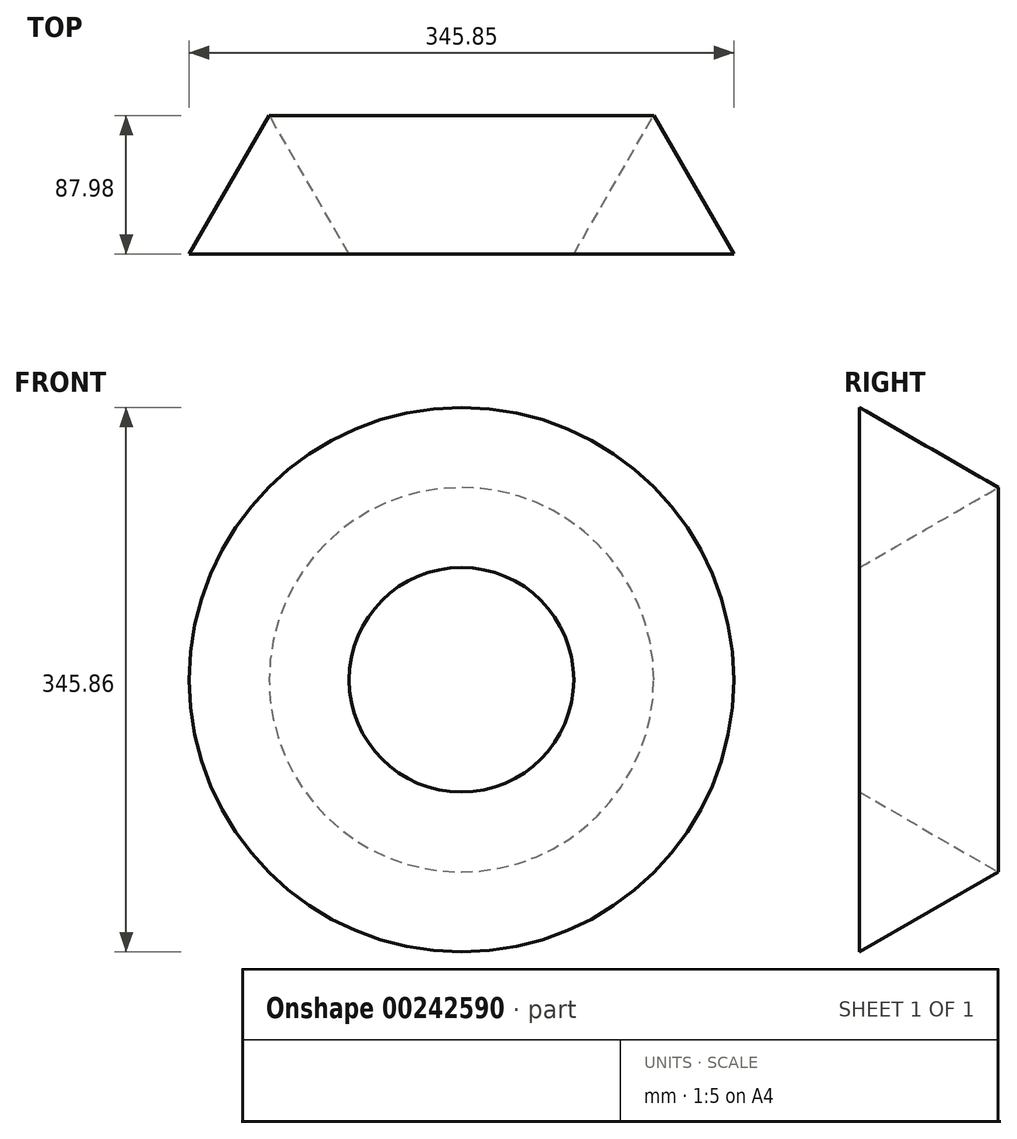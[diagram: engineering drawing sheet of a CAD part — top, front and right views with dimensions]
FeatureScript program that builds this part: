
annotation { "Feature Type Name" : "Feature", "Feature Type Description" : "" }
export const myFeature = defineFeature(function(context is Context, id is Id, definition is map)
    precondition{}
    {
        {
            var Q0;
            Q0=qCreatedBy(makeId("Top.planeOp"),FACE);
            var sketch = newSketch(context, id + "F0", { "sketchPlane" : qUnion([Q0])});
            skLineSegment(sketch, "E0", {"start": v(-50.8, -42.03) * mm, "end": v(0, 45.95) * mm});
            skLineSegment(sketch, "E1", {"start": v(0, 45.95) * mm, "end": v(50.8, -42.03) * mm});
            skLineSegment(sketch, "E2", {"start": v(50.8, -42.03) * mm, "end": v(-50.8, -42.03) * mm});
            skSolve(sketch);
        }
        {
            var Q0;
            Q0=qCreatedBy(makeId("Top.planeOp"),FACE);
            var sketch = newSketch(context, id + "F1", { "sketchPlane" : qUnion([Q0])});
            skLineSegment(sketch, "E3", {"start": v(122.13, 144.23) * mm, "end": v(122.13, -137.17) * mm});
            skSolve(sketch);
        }
        {
            var Q0;
            Q0=makeQuery(id+"F0.imprint","IMPRINT",FACE,{"disambiguationData":[TD([[makeQuery(id+"F0.imprint","IMPRINT",EDGE,{"derivedFrom":sQuery(id+"F0.wireOp",EDGE,"E0")}),-1.0]])]});
            var Q1;
            Q1=sQuery(id+"F1.wireOp",EDGE,"E3");
            revolve(context, id + "F2", {"entities" : qUnion([Q0]), "axis" : qUnion([Q1]), "revolveType" : RevolveType.FULL});
        }
    });
